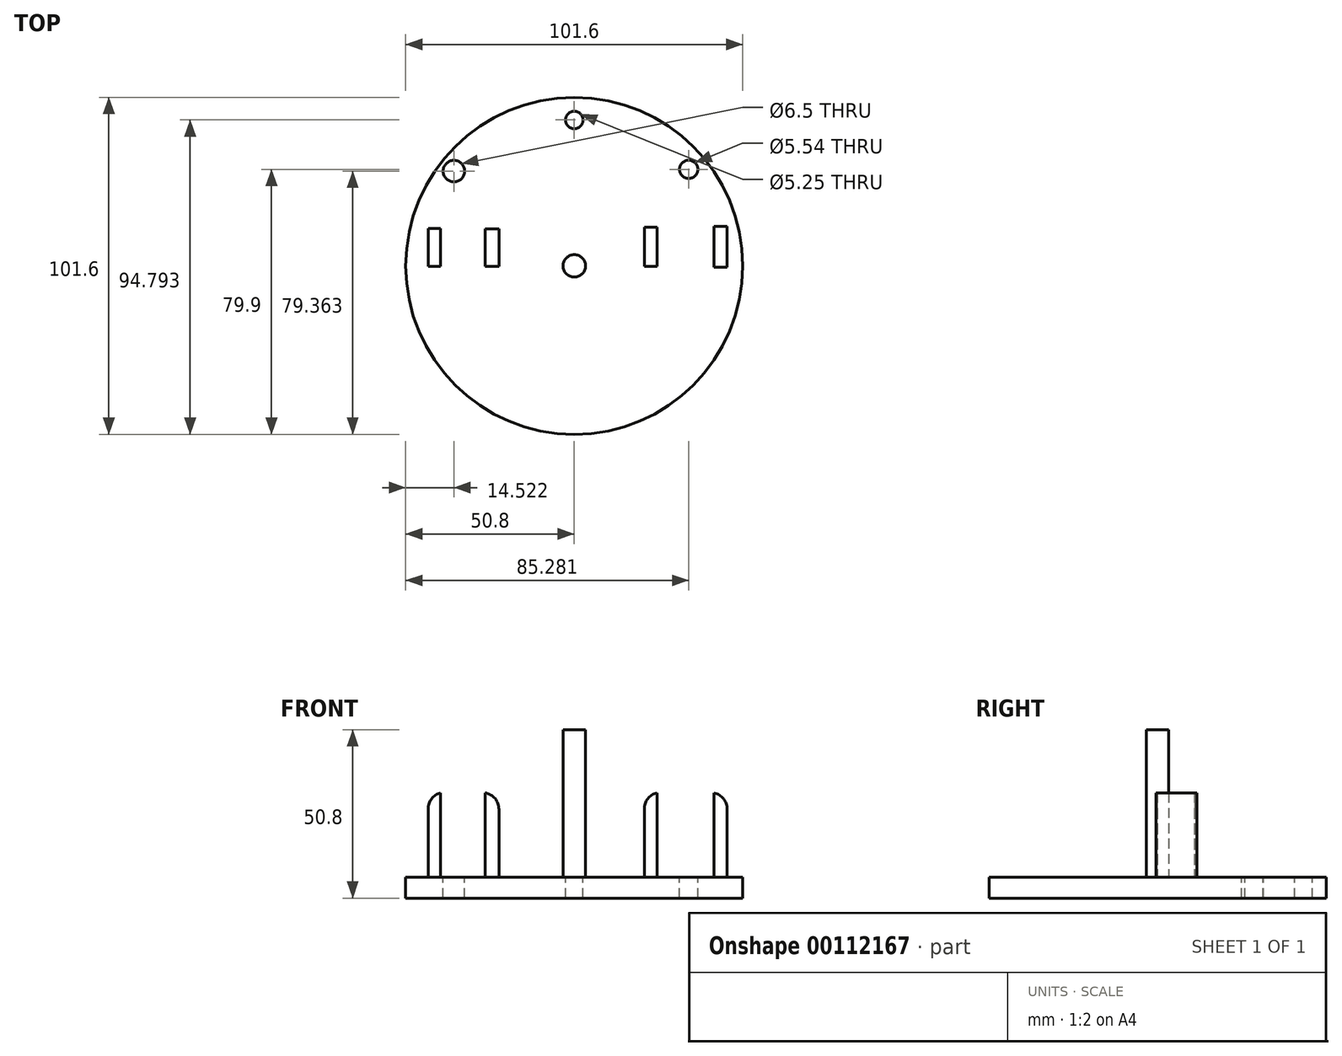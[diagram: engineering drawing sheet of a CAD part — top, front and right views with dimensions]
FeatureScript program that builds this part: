
annotation { "Feature Type Name" : "Feature", "Feature Type Description" : "" }
export const myFeature = defineFeature(function(context is Context, id is Id, definition is map)
    precondition{}
    {
        {
            var Q0;
            Q0=qCreatedBy(makeId("Top.planeOp"),FACE);
            var sketch = newSketch(context, id + "F0", { "sketchPlane" : qUnion([Q0])});
            skCircle(sketch, "E0", {"center": v(0, 0) * mm, "radius": 50.8 * mm});
            skSolve(sketch);
        }
        {
            var Q0;
            Q0 = qSketchRegion(id + "F0", true);
            extrude(context, id + "F1", {"entities" : qUnion([Q0]), "depth" : 6.35 * mm});
        }
        {
            var Q0;
            Q0=qCreatedBy(makeId("Top.planeOp"),FACE);
            var sketch = newSketch(context, id + "F2", { "sketchPlane" : qUnion([Q0])});
            skCircle(sketch, "E1", {"center": v(0, 0) * mm, "radius": 3.39 * mm});
            skSolve(sketch);
        }
        {
            var Q0;
            Q0 = qSketchRegion(id + "F2", true);
            extrude(context, id + "F3", {"entities" : qUnion([Q0]), "operationType" : NewBodyOperationType.ADD, "depth" : 50.8 * mm});
        }
        {
            var Q0;
            Q0=makeQuery(id+"F1.opExtrude","CAP_FACE",FACE,{"disambiguationData":[OSD([sQuery(id+"F0.wireOp",EDGE,"E0")])],"isStart":false});
            var sketch = newSketch(context, id + "F4", { "sketchPlane" : qUnion([Q0])});
            skLineSegment(sketch, "E2.bottom", {"start": v(21.1, 11.66) * mm, "end": v(24.9, 11.66) * mm});
            skLineSegment(sketch, "E2.top", {"start": v(21.1, -0.11) * mm, "end": v(24.9, -0.11) * mm});
            skLineSegment(sketch, "E2.left", {"start": v(21.1, 11.66) * mm, "end": v(21.1, -0.11) * mm});
            skLineSegment(sketch, "E2.right", {"start": v(24.9, 11.66) * mm, "end": v(24.9, -0.11) * mm});
            skLineSegment(sketch, "E3.bottom", {"start": v(42.12, 11.86) * mm, "end": v(46.08, 11.86) * mm});
            skLineSegment(sketch, "E3.top", {"start": v(42.12, -0.43) * mm, "end": v(46.08, -0.43) * mm});
            skLineSegment(sketch, "E3.left", {"start": v(42.12, 11.86) * mm, "end": v(42.12, -0.43) * mm});
            skLineSegment(sketch, "E3.right", {"start": v(46.08, 11.86) * mm, "end": v(46.08, -0.43) * mm});
            skLineSegment(sketch, "E4.bottom", {"start": v(-44.04, 11.3) * mm, "end": v(-40.28, 11.3) * mm});
            skLineSegment(sketch, "E4.top", {"start": v(-44.04, -0.2) * mm, "end": v(-40.28, -0.2) * mm});
            skLineSegment(sketch, "E4.left", {"start": v(-40.28, 11.3) * mm, "end": v(-40.28, -0.2) * mm});
            skLineSegment(sketch, "E4.right", {"start": v(-44.04, 11.3) * mm, "end": v(-44.04, -0.2) * mm});
            skLineSegment(sketch, "E5.bottom", {"start": v(-26.82, 11.14) * mm, "end": v(-22.71, 11.14) * mm});
            skLineSegment(sketch, "E5.top", {"start": v(-26.82, -0.2) * mm, "end": v(-22.71, -0.2) * mm});
            skLineSegment(sketch, "E5.left", {"start": v(-22.71, 11.14) * mm, "end": v(-22.71, -0.2) * mm});
            skLineSegment(sketch, "E5.right", {"start": v(-26.82, 11.14) * mm, "end": v(-26.82, -0.2) * mm});
            skSolve(sketch);
        }
        {
            var Q0;
            Q0 = qSketchRegion(id + "F4", true);
            extrude(context, id + "F5", {"entities" : qUnion([Q0]), "operationType" : NewBodyOperationType.ADD, "depth" : 17.78 * mm});
        }
        {
            var Q0;
            Q0=makeQuery(id+"F5.opExtrude","CAP_EDGE",EDGE,{"disambiguationData":[OSD([sQuery(id+"F4.wireOp",EDGE,"E2.left")])],"isStart":false});
            var Q1;
            Q1=makeQuery(id+"F5.opExtrude","CAP_EDGE",EDGE,{"disambiguationData":[OSD([sQuery(id+"F4.wireOp",EDGE,"E3.right")])],"isStart":false});
            var Q2;
            Q2=makeQuery(id+"F5.opExtrude","CAP_EDGE",EDGE,{"disambiguationData":[OSD([sQuery(id+"F4.wireOp",EDGE,"E2.right")])],"isStart":true});
            var Q3;
            Q3=makeQuery(id+"F5.opExtrude","CAP_EDGE",EDGE,{"disambiguationData":[OSD([sQuery(id+"F4.wireOp",EDGE,"E3.left")])],"isStart":true});
            fillet(context, id + "F6", {"entities" : qUnion([Q0, Q1, Q2, Q3]), "radius" : 5.08 * mm, "tangentPropagation" : true, "allowEdgeOverflow" : false});
        }
        {
            var Q0;
            Q0 = qSketchRegion(id + "F4", true);
            extrude(context, id + "F7", {"entities" : qUnion([Q0]), "operationType" : NewBodyOperationType.ADD, "depth" : 25.4 * mm});
        }
        {
            var Q0;
            Q0=makeQuery(id+"F7.opExtrude","CAP_EDGE",EDGE,{"disambiguationData":[OSD([sQuery(id+"F4.wireOp",EDGE,"E4.right")])],"isStart":false});
            var Q1;
            Q1=makeQuery(id+"F5.opExtrude","CAP_EDGE",EDGE,{"disambiguationData":[OSD([sQuery(id+"F4.wireOp",EDGE,"E5.right")])],"isStart":true});
            var Q2;
            Q2=makeQuery(id+"F7.opExtrude","CAP_EDGE",EDGE,{"disambiguationData":[OSD([sQuery(id+"F4.wireOp",EDGE,"E5.left")])],"isStart":false});
            var Q3;
            Q3=makeQuery(id+"F7.opExtrude","CAP_EDGE",EDGE,{"disambiguationData":[OSD([sQuery(id+"F4.wireOp",EDGE,"E2.left")])],"isStart":false});
            var Q4;
            Q4=makeQuery(id+"F7.opExtrude","CAP_EDGE",EDGE,{"disambiguationData":[OSD([sQuery(id+"F4.wireOp",EDGE,"E3.right")])],"isStart":false});
            var Q5;
            Q5=makeQuery(id+"F5.opExtrude","CAP_EDGE",EDGE,{"disambiguationData":[OSD([sQuery(id+"F4.wireOp",EDGE,"E4.left")])],"isStart":true});
            fillet(context, id + "F8", {"entities" : qUnion([Q0, Q1, Q2, Q3, Q4, Q5]), "radius" : 5.08 * mm, "tangentPropagation" : true, "allowEdgeOverflow" : false});
        }
        {
            var Q0;
            Q0=makeQuery(id+"F1.opExtrude","CAP_FACE",FACE,{"disambiguationData":[OSD([sQuery(id+"F0.wireOp",EDGE,"E0")])],"isStart":false});
            var sketch = newSketch(context, id + "F9", { "sketchPlane" : qUnion([Q0])});
            skCircle(sketch, "E6", {"center": v(0, 44) * mm, "radius": 2.62 * mm});
            skCircle(sketch, "E7", {"center": v(34.48, 29.1) * mm, "radius": 2.77 * mm});
            skCircle(sketch, "E8", {"center": v(-36.28, 28.56) * mm, "radius": 3.25 * mm});
            skSolve(sketch);
        }
        {
            var Q0;
            Q0 = qSketchRegion(id + "F9", true);
            extrude(context, id + "F10", {"entities" : qUnion([Q0]), "operationType" : NewBodyOperationType.REMOVE, "oppositeDirection" : true, "depth" : 25.4 * mm});
        }
    });
